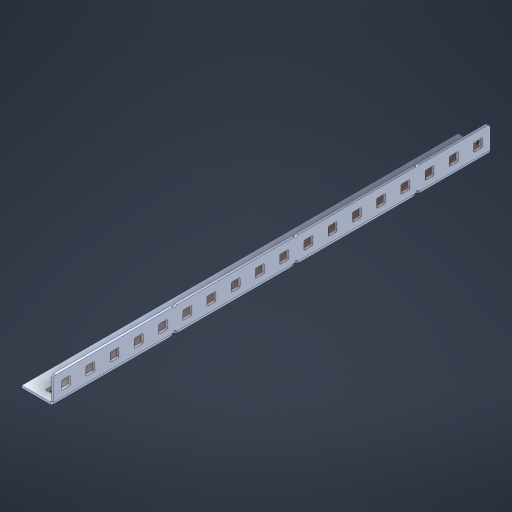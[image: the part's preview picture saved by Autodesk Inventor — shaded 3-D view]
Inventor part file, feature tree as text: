
AUTODESK INVENTOR PART (.ipt)
format: ipt  version: 2023 (Build 270158000, 158)  size: 715,776 bytes
history: native  units: in
note: dims shown in document units (in); Inventor stores cm internally (conversion verified against a paired STEP export)
features: other x41, extrude x35, sheet_metal_op x10, sketch x8, mirror x1, pattern_linear x1, chamfer x1
ambient origin geometry x8: Origin, YZ Plane, XZ Plane, XY Plane, X Axis, Y Axis, Z Axis, Center Point
bodies: Solid1 (feature_tree), Body (feature_tree)
feature tree (97):
  other  "Flange Pattern Plane"
  sheet_metal_op  "Flange Pattern"
  sheet_metal_op  "Body Pattern"
  other  "Arc Length"
  mirror  "Notch Mirror"
  pattern_linear  "Notch Pattern"  Spacing1=0.1875in  [1 undecoded]
  chamfer  "End Chamfer"
  extrude  "Half Cut"  Depth=0.0469in
  sketch  "Sketch1"  dims[d0=2.5in]
  other  "Plate1"
  sketch  "Sketch2"  dims[d1=9.0in]
  other  "Plate2"
  sheet_metal_op  "Bend1"
  sheet_metal_op  "Corner1"
  sketch  "Sketch3"  dims[d2=0.0469in]
  other  "Flange Pattern Sketch"
  sketch  "Sketch7"  dims[d3=0.0469in]
  other  "Srf1"
  other  "Srf2"
  sketch  "Sketch8"  dims[d4=0.0234in]
  sketch  "Sketch9"  dims[d5=0.0938in]
  other  "Srf91"
  sheet_metal_op  "Body Pattern Sketch"
  other  "Srf92"
  sketch  "Sketch13"  dims[d6=0.0469in]
  sketch  "Sketch14"  dims[d7=0.5in d8=90.0deg d9=0.0312in d10=0.1875in d11=0.0469in d12=0.0469in d16=0.182in d17=0.02in d18=0.0469in d19=0.0in d20=0.25in d21=0.25in d46=0.172in d47=1.0in d48=0.0in d49=0.182in d50=0.02in d51=0.25in d52=0.25in d53=0.0469in d54=0.0in d55=0.172in d56=1.0in d57=0.0in d60=7.0866in d62=0.5in d63=0.3937in d65=0.5in d85=0.1227in d86=0.1659in d88=0.04in d89=0.0469in d90=0.0in d91=0.04in d92=0.0491in d95=2.5in d96=0.04in d97=0.25in d98=45.0deg d101=0.0in d102=2.497in d131=0.5in d132=7.0866in d134=0.5in d139=0.5in]
  other  "Srf856"
  other  "Srf1310"
  other  "Srf1311"
  other  "Srf1312"
  other  "Srf1376"
  other  "Srf1377"
  other  "Srf1728"
  other  "Srf1755"
  other  "Srf1878"
  other  "Srf1879"
  other  "Srf1880"
  other  "Srf1881"
  other  "Srf1882"
  other  "Srf1883"
  other  "Srf1884"
  other  "Srf1885"
  other  "Srf1886"
  other  "Srf1887"
  other  "Srf1888"
  other  "Srf1889"
  other  "Srf1942"
  other  "Srf1943"
  other  "Srf1944"
  other  "Srf1945"
  other  "Srf1946"
  other  "Srf1947"
  other  "Srf1948"
  other  "Srf1949"
  other  "Srf1950"
  other  "Srf1951"
  other  "Srf1952"
  other  "Srf1953"
  sheet_metal_op  "Flange Stamp"
  sheet_metal_op  "Flange Circle"
  sheet_metal_op  "Body Stamp"
  sheet_metal_op  "Body Circle"
  sheet_metal_op  "Notch"
  extrude  "ExtrusionSrf2"  Depth=0.0469in
  extrude  "ExtrusionSrf92"  Depth=0.5in
  extrude  "ExtrusionSrf856"  Depth=0.02in
  extrude  "ExtrusionSrf1310"  Depth=0.0469in
  extrude  "ExtrusionSrf1311"  TaperAngle=0.0deg  [1 undecoded]
  extrude  "ExtrusionSrf1312"  Depth=0.5in
  extrude  "ExtrusionSrf1376"  Depth=0.5in
  extrude  "ExtrusionSrf1377"  Depth=0.5in
  extrude  "ExtrusionSrf1728"  Depth=0.5in TaperAngle=0.0deg
  extrude  "ExtrusionSrf1755"  Depth=0.5in
  extrude  "ExtrusionSrf1878"  Depth=0.02in
  extrude  "ExtrusionSrf1879"  Depth=0.5in
  extrude  "ExtrusionSrf1880"  Depth=0.5in
  extrude  "ExtrusionSrf1881"  Depth=0.0469in
  extrude  "ExtrusionSrf1882"  TaperAngle=0.0deg  [1 undecoded]
  extrude  "ExtrusionSrf1883"  Depth=0.5in
  extrude  "ExtrusionSrf1884"  Depth=0.5in TaperAngle=0.0deg
  extrude  "ExtrusionSrf1885"  Depth=0.5in
  extrude  "ExtrusionSrf1886"  Depth=0.5in
  extrude  "ExtrusionSrf1887"  Depth=0.5in
  extrude  "ExtrusionSrf1888"  Depth=0.5in
  extrude  "ExtrusionSrf1889"  Depth=0.5in
  extrude  "ExtrusionSrf1942"  Depth=0.0469in
  extrude  "ExtrusionSrf1943"  TaperAngle=0.0deg  [1 undecoded]
  extrude  "ExtrusionSrf1944"  Depth=0.5in
  extrude  "ExtrusionSrf1945"  Depth=0.5in
  extrude  "ExtrusionSrf1946"  Depth=0.5in
  extrude  "ExtrusionSrf1947"  Depth=0.5in TaperAngle=45.0deg
  extrude  "ExtrusionSrf1948"  TaperAngle=0.0deg  [1 undecoded]
  extrude  "ExtrusionSrf1949"  Depth=0.5in
  extrude  "ExtrusionSrf1950"  Depth=0.5in
  extrude  "ExtrusionSrf1951"  Depth=0.5in
  extrude  "ExtrusionSrf1952"  Depth=0.5in
  extrude  "ExtrusionSrf1953"  Depth=0.5in
note: 5 required parameter values undecoded (feature->parameter linkage not recoverable at this tier; creation-order binding heuristic only, values carry confidence <= 0.55)
